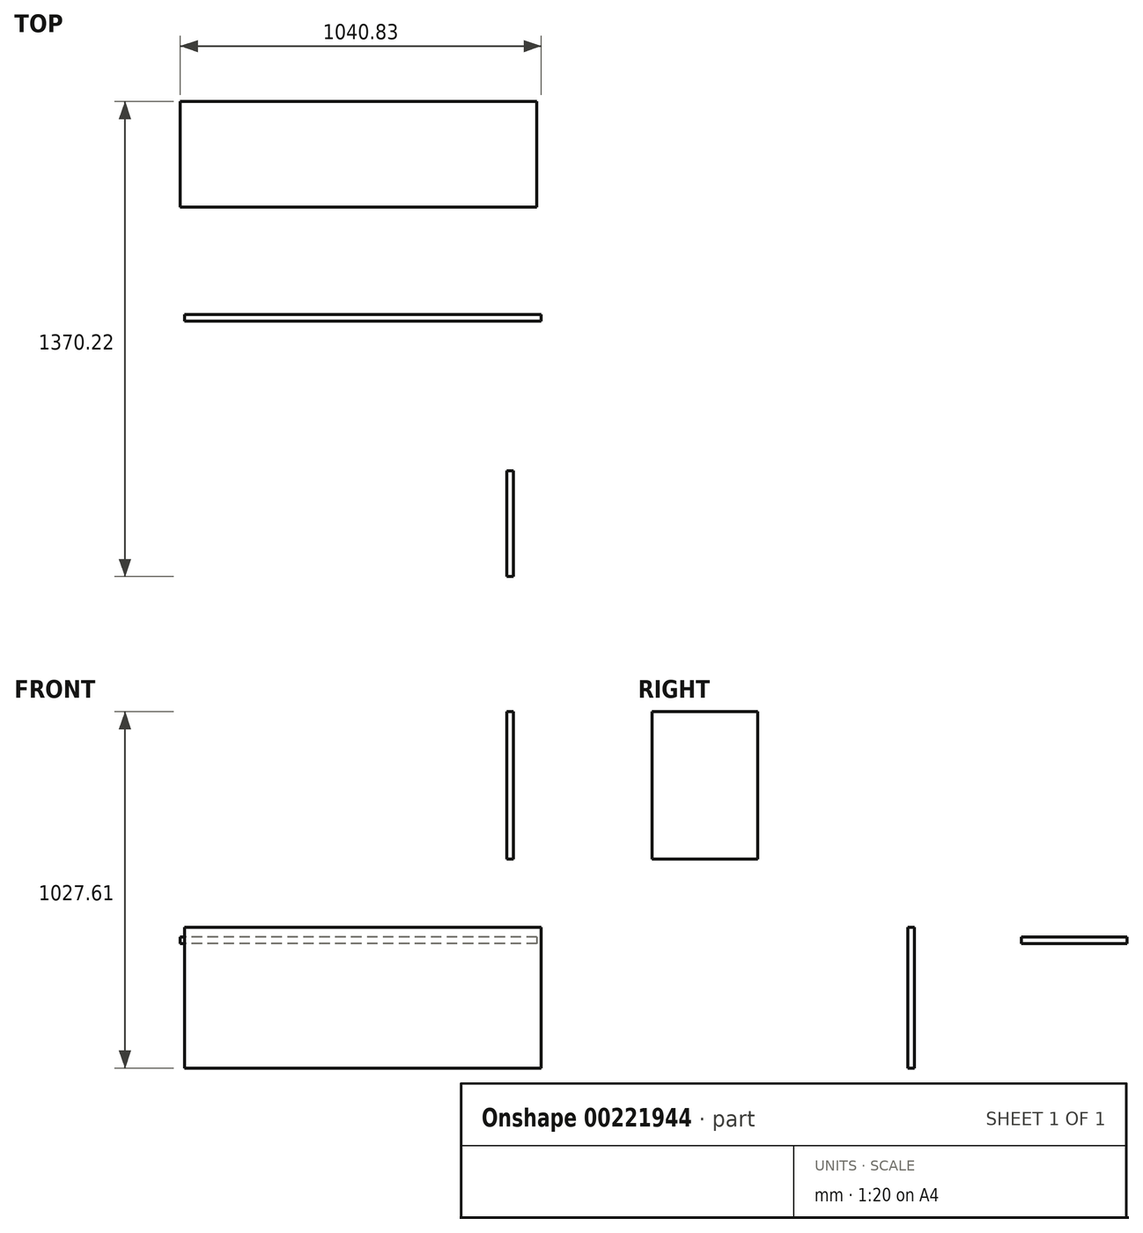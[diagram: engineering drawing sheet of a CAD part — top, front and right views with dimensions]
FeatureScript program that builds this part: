
annotation { "Feature Type Name" : "Feature", "Feature Type Description" : "" }
export const myFeature = defineFeature(function(context is Context, id is Id, definition is map)
    precondition{}
    {
        {
            var Q0;
            Q0=qCreatedBy(makeId("Front.planeOp"),FACE);
            var sketch = newSketch(context, id + "F0", { "sketchPlane" : qUnion([Q0])});
            skLineSegment(sketch, "E0.bottom", {"start": v(-929.47, 47.67) * mm, "end": v(99.23, 47.67) * mm});
            skLineSegment(sketch, "E0.top", {"start": v(-929.47, -358.73) * mm, "end": v(99.23, -358.73) * mm});
            skLineSegment(sketch, "E0.left", {"start": v(-929.47, 47.67) * mm, "end": v(-929.47, -358.73) * mm});
            skLineSegment(sketch, "E0.right", {"start": v(99.23, 47.67) * mm, "end": v(99.23, -358.73) * mm});
            skSolve(sketch);
        }
        {
            var Q0;
            Q0 = qSketchRegion(id + "F0", true);
            extrude(context, id + "F1", {"entities" : qUnion([Q0]), "depth" : 19.05 * mm});
        }
        {
            var Q0;
            Q0=qCreatedBy(makeId("Top.planeOp"),FACE);
            var sketch = newSketch(context, id + "F2", { "sketchPlane" : qUnion([Q0])});
            skLineSegment(sketch, "E1.bottom", {"start": v(87.1, 308.73) * mm, "end": v(-941.6, 308.73) * mm});
            skLineSegment(sketch, "E1.top", {"start": v(87.1, 613.53) * mm, "end": v(-941.6, 613.53) * mm});
            skLineSegment(sketch, "E1.left", {"start": v(87.1, 308.73) * mm, "end": v(87.1, 613.53) * mm});
            skLineSegment(sketch, "E1.right", {"start": v(-941.6, 308.73) * mm, "end": v(-941.6, 613.53) * mm});
            skSolve(sketch);
        }
        {
            var Q0;
            Q0 = qSketchRegion(id + "F2", true);
            extrude(context, id + "F3", {"entities" : qUnion([Q0]), "depth" : 19.05 * mm});
        }
        {
            var Q0;
            Q0=qCreatedBy(makeId("Right.planeOp"),FACE);
            var sketch = newSketch(context, id + "F4", { "sketchPlane" : qUnion([Q0])});
            skLineSegment(sketch, "E2.bottom", {"start": v(-451.89, 243.43) * mm, "end": v(-756.69, 243.43) * mm});
            skLineSegment(sketch, "E2.top", {"start": v(-451.89, 668.88) * mm, "end": v(-756.69, 668.88) * mm});
            skLineSegment(sketch, "E2.left", {"start": v(-451.89, 243.43) * mm, "end": v(-451.89, 668.88) * mm});
            skLineSegment(sketch, "E2.right", {"start": v(-756.69, 243.43) * mm, "end": v(-756.69, 668.88) * mm});
            skSolve(sketch);
        }
        {
            var Q0;
            Q0 = qSketchRegion(id + "F4", true);
            extrude(context, id + "F5", {"entities" : qUnion([Q0]), "depth" : 19.05 * mm});
        }
    });
